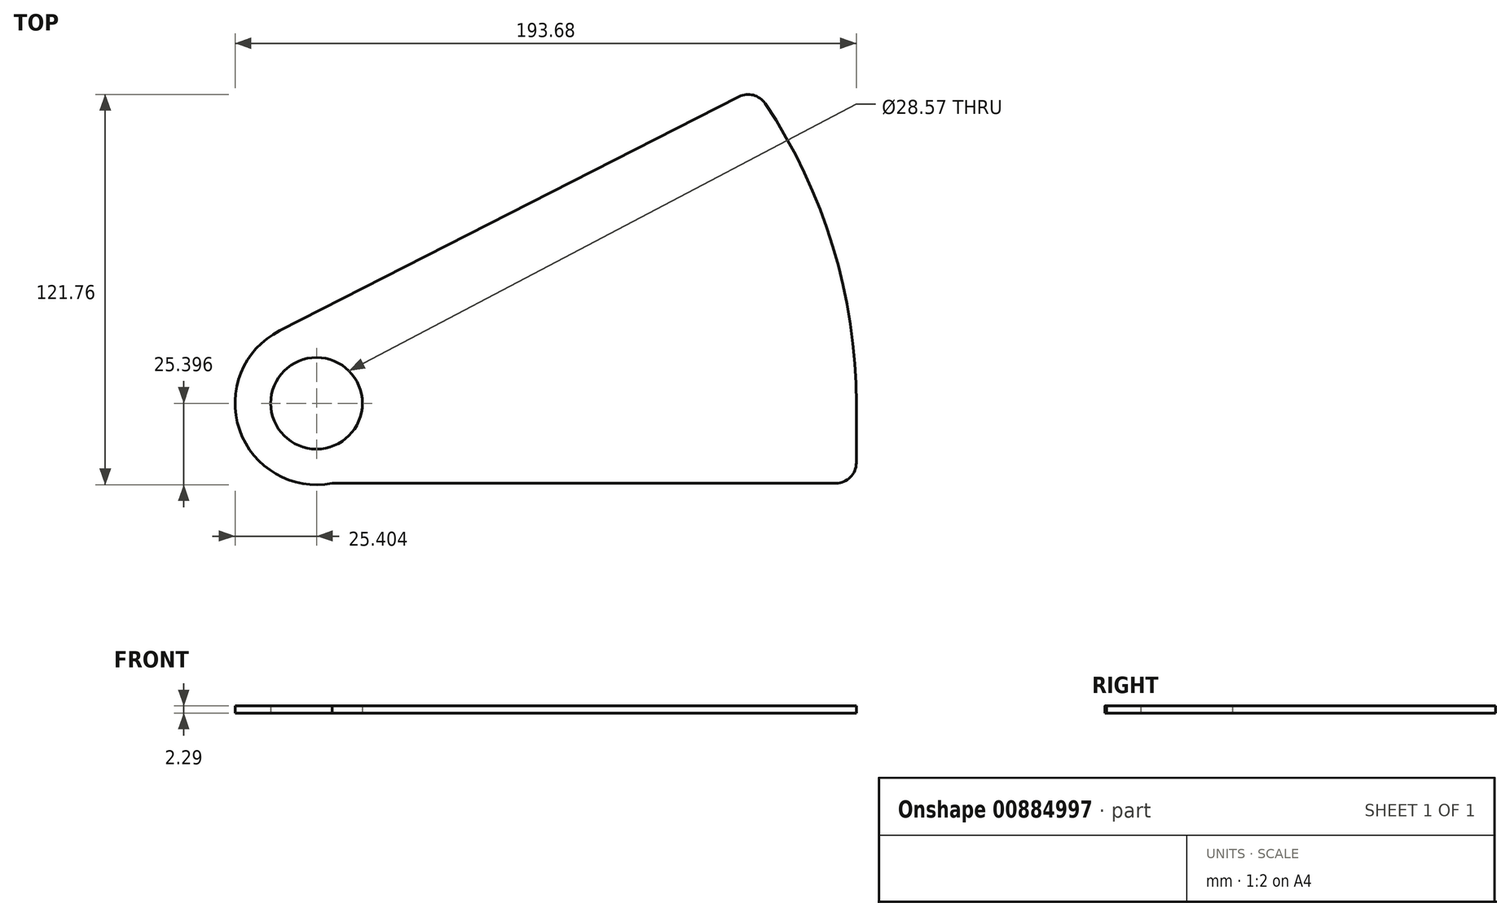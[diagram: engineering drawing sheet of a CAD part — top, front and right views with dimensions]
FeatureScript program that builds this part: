
annotation { "Feature Type Name" : "Feature", "Feature Type Description" : "" }
export const myFeature = defineFeature(function(context is Context, id is Id, definition is map)
    precondition{}
    {
        {
            var Q0;
            Q0=qCreatedBy(makeId("Top.planeOp"),FACE);
            var sketch = newSketch(context, id + "F0", { "sketchPlane" : qUnion([Q0])});
            skCircle(sketch, "E0", {"center": v(-13.22, -97.56) * mm, "radius": 14.29 * mm});
            skCircle(sketch, "E1", {"center": v(-13.22, -97.56) * mm, "radius": 25.4 * mm});
            skLineSegment(sketch, "E2", {"start": v(-13.18, -122.5) * mm, "end": v(-8.87, -122.59) * mm});
            skArc(sketch, "E3", {"start": v(155.06, -97.56) * mm, "mid": v(147.8, -48.68) * mm, "end": v(126.66, -4.02) * mm});
            skLineSegment(sketch, "E4", {"start": v(155.06, -116.15) * mm, "end": v(155.06, -97.56) * mm});
            skLineSegment(sketch, "E5", {"start": v(118.5, -1.9) * mm, "end": v(-24.75, -74.94) * mm});
            skPoint(sketch, "E6.visualSharp", {"position": v(155.06, -126.14) * mm});
            skPoint(sketch, "E7.visualSharp", {"position": v(123.44, 0.63) * mm});
            skArc(sketch, "E7.filletArc", {"start": v(126.66, -4.02) * mm, "mid": v(122.98, -1.4) * mm, "end": v(118.5, -1.9) * mm});
            skArc(sketch, "E8", {"start": v(148.65, -97.56) * mm, "mid": v(137, -37.3) * mm, "end": v(103.76, 14.3) * mm});
            skLineSegment(sketch, "E9", {"start": v(-38.6, -96.55) * mm, "end": v(-38.62, -97.56) * mm});
            skLineSegment(sketch, "E10", {"start": v(-13.2, -122.5) * mm, "end": v(-13.18, -122.5) * mm});
            skLineSegment(sketch, "E11", {"start": v(148.65, -97.56) * mm, "end": v(148.65, -122.5) * mm});
            skPoint(sketch, "E12.visualSharp", {"position": v(-39.16, -122.5) * mm});
            skArc(sketch, "E12.filletArc", {"start": v(-38.6, -96.55) * mm, "mid": v(-31.35, -114.86) * mm, "end": v(-13.2, -122.5) * mm});
            skLineSegment(sketch, "E13", {"start": v(-13.18, -122.5) * mm, "end": v(148.7, -122.5) * mm});
            skPoint(sketch, "E14.visualSharp", {"position": v(155.06, -122.5) * mm});
            skArc(sketch, "E14.filletArc", {"start": v(148.7, -122.5) * mm, "mid": v(153.2, -120.64) * mm, "end": v(155.06, -116.15) * mm});
            skSolve(sketch);
        }
        {
            var Q0;
            Q0 = qSketchRegion(id + "F0", true);
            extrude(context, id + "F1", {"entities" : qUnion([Q0]), "depth" : 2.3 * mm, "offsetDistance" : 25.4 * mm});
        }
    });
